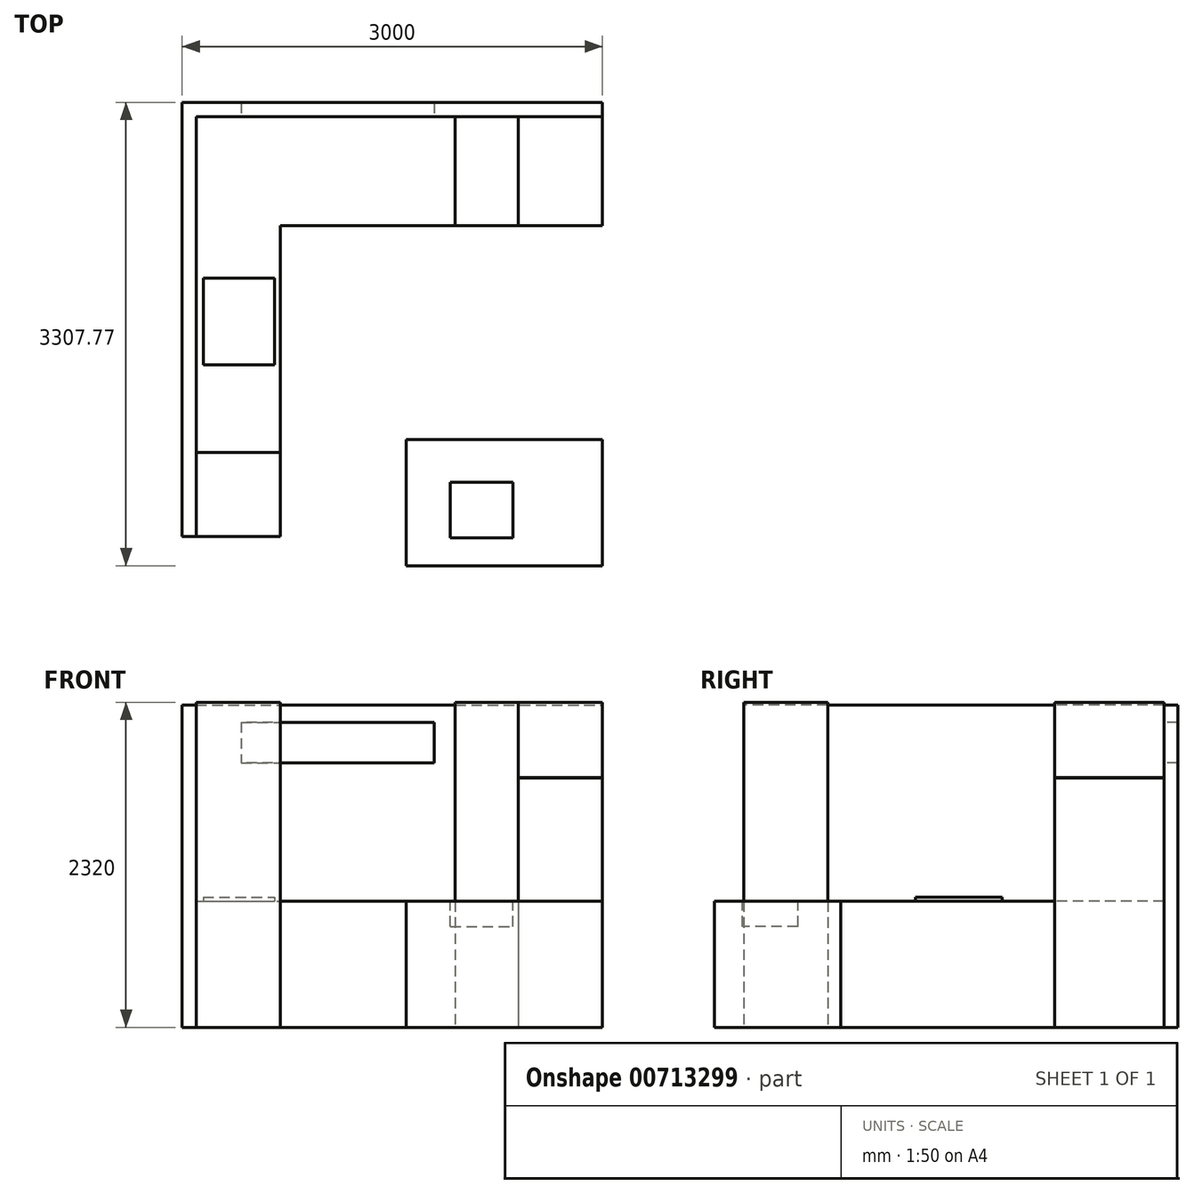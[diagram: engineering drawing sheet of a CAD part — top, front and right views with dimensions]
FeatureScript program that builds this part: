
annotation { "Feature Type Name" : "Feature", "Feature Type Description" : "" }
export const myFeature = defineFeature(function(context is Context, id is Id, definition is map)
    precondition{}
    {
        {
            var Q0;
            Q0=qCreatedBy(makeId("Top.planeOp"),FACE);
            var sketch = newSketch(context, id + "F0", { "sketchPlane" : qUnion([Q0])});
            skLineSegment(sketch, "E0.bottom", {"start": v(-1814.68, 1638.26) * mm, "end": v(1085.32, 1638.26) * mm});
            skLineSegment(sketch, "E0.left", {"start": v(-1814.68, 1638.26) * mm, "end": v(-1814.68, 1038.26) * mm});
            skLineSegment(sketch, "E0.right", {"start": v(1085.32, 1638.26) * mm, "end": v(1085.32, 858.26) * mm});
            skLineSegment(sketch, "E1", {"start": v(-1814.68, 1038.26) * mm, "end": v(-1814.68, -1361.74) * mm});
            skLineSegment(sketch, "E2", {"start": v(-1814.68, -1361.74) * mm, "end": v(-1214.68, -1361.74) * mm});
            skLineSegment(sketch, "E3", {"start": v(-1214.68, -1361.74) * mm, "end": v(-1214.68, 858.26) * mm});
            skLineSegment(sketch, "E4", {"start": v(-1214.68, 858.26) * mm, "end": v(1085.32, 858.26) * mm});
            skLineSegment(sketch, "E5", {"start": v(485.32, 1638.26) * mm, "end": v(485.32, 858.26) * mm});
            skLineSegment(sketch, "E6", {"start": v(35.32, 1638.26) * mm, "end": v(35.32, 858.26) * mm});
            skLineSegment(sketch, "E7", {"start": v(-1814.68, -761.74) * mm, "end": v(-1214.68, -761.74) * mm});
            skLineSegment(sketch, "E8.bottom", {"start": v(-314.68, -669.51) * mm, "end": v(1085.32, -669.51) * mm});
            skLineSegment(sketch, "E8.top", {"start": v(-314.68, -1569.51) * mm, "end": v(1085.32, -1569.51) * mm});
            skLineSegment(sketch, "E8.left", {"start": v(-314.68, -669.51) * mm, "end": v(-314.68, -1569.51) * mm});
            skLineSegment(sketch, "E8.right", {"start": v(1085.32, -669.51) * mm, "end": v(1085.32, -1569.51) * mm});
            skLineSegment(sketch, "E9.0", {"start": v(-1914.68, 1738.26) * mm, "end": v(1085.32, 1738.26) * mm});
            skLineSegment(sketch, "E9.1", {"start": v(-1914.68, 1738.26) * mm, "end": v(-1914.68, 858.26) * mm});
            skLineSegment(sketch, "E9.2", {"start": v(-1914.68, 858.26) * mm, "end": v(-1914.68, -1361.74) * mm});
            skLineSegment(sketch, "E10", {"start": v(1085.32, 1638.26) * mm, "end": v(1085.32, 1738.26) * mm});
            skLineSegment(sketch, "E11", {"start": v(-1814.68, -1361.74) * mm, "end": v(-1914.68, -1361.74) * mm});
            skLineSegment(sketch, "E12", {"start": v(-1914.68, -1361.74) * mm, "end": v(-1814.68, -1361.74) * mm});
            skSolve(sketch);
        }
        {
            var Q0;
            {var subQ0=sQuery(id+"F0.wireOp",EDGE,"E0.right");Q0=makeQuery(id+"F0.imprint","IMPRINT",FACE,{"disambiguationData":[TD([[makeQuery(id+"F0.imprint","IMPRINT",EDGE,{"derivedFrom":subQ0}),-1.0]])]});}
            extrude(context, id + "F1", {"entities" : qUnion([Q0]), "depth" : 1780 * mm, "offsetDistance" : 25 * mm});
        }
        {
            var Q0;
            {var subQ0=sQuery(id+"F0.wireOp",EDGE,"E5");Q0=makeQuery(id+"F0.imprint","IMPRINT",FACE,{"disambiguationData":[TD([[makeQuery(id+"F0.imprint","IMPRINT",EDGE,{"derivedFrom":subQ0}),-1.0]])]});}
            extrude(context, id + "F2", {"entities" : qUnion([Q0]), "depth" : 2320 * mm, "offsetDistance" : 25 * mm});
        }
        {
            var Q0;
            {var subQ0=sQuery(id+"F0.wireOp",EDGE,"E2");Q0=makeQuery(id+"F0.imprint","IMPRINT",FACE,{"disambiguationData":[TD([[makeQuery(id+"F0.imprint","IMPRINT",EDGE,{"derivedFrom":subQ0}),1.0]])]});}
            extrude(context, id + "F3", {"entities" : qUnion([Q0]), "depth" : 2320 * mm, "offsetDistance" : 25 * mm});
        }
        {
            var Q0;
            {var subQ4=sQuery(id+"F0.wireOp",EDGE,"E0.left");Q0=makeQuery(id+"F0.imprint","IMPRINT",FACE,{"disambiguationData":[TD([[makeQuery(id+"F0.imprint","IMPRINT",EDGE,{"derivedFrom":subQ4}),1.0]])]});}
            extrude(context, id + "F4", {"entities" : qUnion([Q0]), "depth" : 900 * mm, "offsetDistance" : 25 * mm});
        }
        {
            var Q0;
            Q0=makeQuery(id+"F0.imprint","IMPRINT",FACE,{"disambiguationData":[TD([[makeQuery(id+"F0.imprint","IMPRINT",EDGE,{"derivedFrom":sQuery(id+"F0.wireOp",EDGE,"E8.bottom")}),-1.0]])]});
            extrude(context, id + "F5", {"entities" : qUnion([Q0]), "depth" : 900 * mm, "offsetDistance" : 25 * mm});
        }
        {
            var Q0;
            Q0=makeQuery(id+"F2.opExtrude","SWEPT_FACE",FACE,{"disambiguationData":[OSD([sQuery(id+"F0.wireOp",EDGE,"E5")])]});
            var sketch = newSketch(context, id + "F6", { "sketchPlane" : qUnion([Q0])});
            skLineSegment(sketch, "E13.bottom", {"start": v(858.26, 2320) * mm, "end": v(1638.26, 2320) * mm});
            skLineSegment(sketch, "E13.top", {"start": v(858.26, 1782.28) * mm, "end": v(1638.26, 1782.28) * mm});
            skLineSegment(sketch, "E13.left", {"start": v(858.26, 2320) * mm, "end": v(858.26, 1782.28) * mm});
            skLineSegment(sketch, "E13.right", {"start": v(1638.26, 2320) * mm, "end": v(1638.26, 1782.28) * mm});
            skSolve(sketch);
        }
        {
            var Q0;
            Q0 = qSketchRegion(id + "F6", true);
            extrude(context, id + "F7", {"entities" : qUnion([Q0]), "depth" : 600 * mm, "offsetDistance" : 25 * mm});
        }
        {
            var Q0;
            {var subQ3=sQuery(id+"F0.wireOp",EDGE,"E0.left");Q0=makeQuery(id+"F0.imprint","IMPRINT",FACE,{"disambiguationData":[TD([[makeQuery(id+"F0.imprint","IMPRINT",EDGE,{"derivedFrom":subQ3}),-1.0]])]});}
            extrude(context, id + "F8", {"entities" : qUnion([Q0]), "depth" : 2300 * mm, "offsetDistance" : 25 * mm});
        }
        {
            var Q0;
            Q0=makeQuery(id+"F4.opExtrude","CAP_FACE",FACE,{"disambiguationData":[OSD([sQuery(id+"F0.wireOp",EDGE,"E0.bottom"),sQuery(id+"F0.wireOp",EDGE,"E0.left"),sQuery(id+"F0.wireOp",EDGE,"E1"),sQuery(id+"F0.wireOp",EDGE,"E3"),sQuery(id+"F0.wireOp",EDGE,"E4"),sQuery(id+"F0.wireOp",EDGE,"E6"),sQuery(id+"F0.wireOp",EDGE,"E7")])],"isStart":false});
            var sketch = newSketch(context, id + "F9", { "sketchPlane" : qUnion([Q0])});
            skLineSegment(sketch, "E14.bottom", {"start": v(-1764.68, -134.6) * mm, "end": v(-1254.68, -134.6) * mm});
            skLineSegment(sketch, "E14.top", {"start": v(-1764.68, 485.4) * mm, "end": v(-1254.68, 485.4) * mm});
            skLineSegment(sketch, "E14.left", {"start": v(-1764.68, -134.6) * mm, "end": v(-1764.68, 485.4) * mm});
            skLineSegment(sketch, "E14.right", {"start": v(-1254.68, -134.6) * mm, "end": v(-1254.68, 485.4) * mm});
            skSolve(sketch);
        }
        {
            var Q0;
            Q0=makeQuery(id+"F9.imprint","IMPRINT",FACE,{"disambiguationData":[TD([[makeQuery(id+"F9.imprint","IMPRINT",EDGE,{"derivedFrom":sQuery(id+"F9.wireOp",EDGE,"E14.bottom")}),1.0]])]});
            extrude(context, id + "F10", {"entities" : qUnion([Q0]), "depth" : 28 * mm, "offsetDistance" : 25 * mm});
        }
        {
            var Q0;
            Q0=makeQuery(id+"F8.opExtrude","SWEPT_FACE",FACE,{"disambiguationData":[OSD([sQuery(id+"F0.wireOp",EDGE,"E0.bottom")])]});
            var sketch = newSketch(context, id + "F11", { "sketchPlane" : qUnion([Q0])});
            skLineSegment(sketch, "E15.bottom", {"start": v(-1492.73, 2178.25) * mm, "end": v(-117.04, 2178.25) * mm});
            skLineSegment(sketch, "E15.top", {"start": v(-1492.73, 1889.02) * mm, "end": v(-117.04, 1889.02) * mm});
            skLineSegment(sketch, "E15.left", {"start": v(-1492.73, 2178.25) * mm, "end": v(-1492.73, 1889.02) * mm});
            skLineSegment(sketch, "E15.right", {"start": v(-117.04, 2178.25) * mm, "end": v(-117.04, 1889.02) * mm});
            skSolve(sketch);
        }
        {
            var Q0;
            Q0 = qSketchRegion(id + "F11", true);
            var Q1;
            Q1=makeQuery(id+"F11.imprint","IMPRINT",FACE,{"disambiguationData":[TD([[makeQuery(id+"F11.imprint","IMPRINT",EDGE,{"derivedFrom":sQuery(id+"F11.wireOp",EDGE,"E15.bottom")}),-1.0]])]});
            extrude(context, id + "F12", {"entities" : qUnion([Q0, Q1]), "operationType" : NewBodyOperationType.REMOVE, "endBound" : BoundingType.THROUGH_ALL, "oppositeDirection" : true, "depth" : 25 * mm, "offsetDistance" : 25 * mm});
        }
        {
            var Q0;
            Q0=makeQuery(id+"F5.opExtrude","CAP_FACE",FACE,{"disambiguationData":[OSD([sQuery(id+"F0.wireOp",EDGE,"E8.bottom"),sQuery(id+"F0.wireOp",EDGE,"E8.top"),sQuery(id+"F0.wireOp",EDGE,"E8.left"),sQuery(id+"F0.wireOp",EDGE,"E8.right")])],"isStart":false});
            var sketch = newSketch(context, id + "F13", { "sketchPlane" : qUnion([Q0])});
            skLineSegment(sketch, "E16.bottom", {"start": v(0, -974.51) * mm, "end": v(445, -974.51) * mm});
            skLineSegment(sketch, "E16.top", {"start": v(0, -1369.51) * mm, "end": v(445, -1369.51) * mm});
            skLineSegment(sketch, "E16.left", {"start": v(0, -974.51) * mm, "end": v(0, -1369.51) * mm});
            skLineSegment(sketch, "E16.right", {"start": v(445, -974.51) * mm, "end": v(445, -1369.51) * mm});
            skSolve(sketch);
        }
        {
            var Q0;
            Q0=makeQuery(id+"F13.imprint","IMPRINT",FACE,{"disambiguationData":[TD([[makeQuery(id+"F13.imprint","IMPRINT",EDGE,{"derivedFrom":sQuery(id+"F13.wireOp",EDGE,"E16.bottom")}),-1.0]])]});
            extrude(context, id + "F14", {"entities" : qUnion([Q0]), "operationType" : NewBodyOperationType.REMOVE, "oppositeDirection" : true, "depth" : 180 * mm, "offsetDistance" : 25 * mm});
        }
    });
